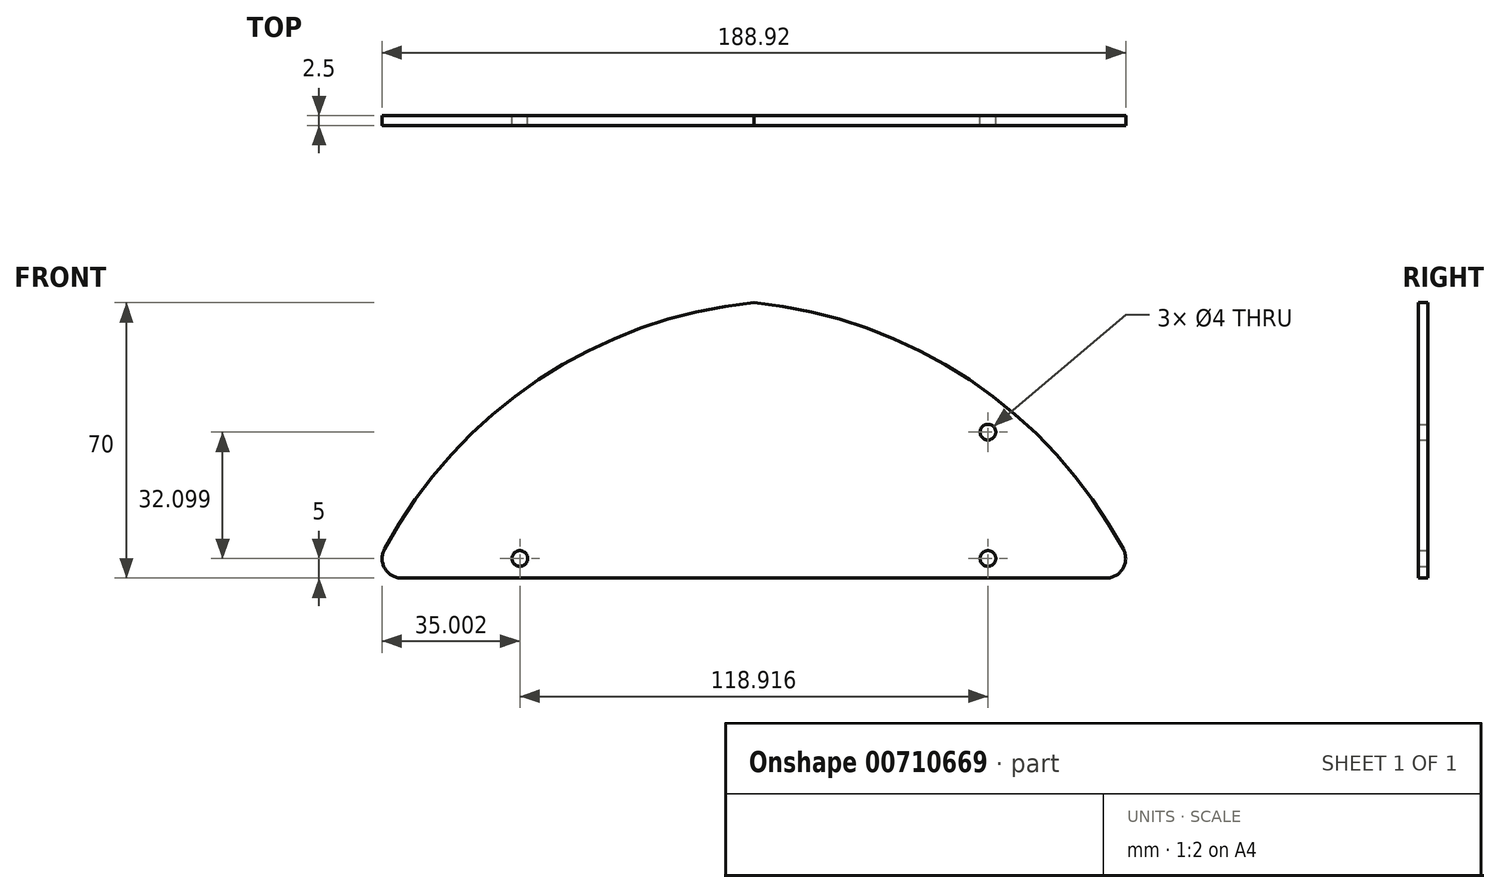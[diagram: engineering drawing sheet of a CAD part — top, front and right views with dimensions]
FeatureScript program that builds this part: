
annotation { "Feature Type Name" : "Feature", "Feature Type Description" : "" }
export const myFeature = defineFeature(function(context is Context, id is Id, definition is map)
    precondition{}
    {
        {
            var Q0;
            Q0=qCreatedBy(makeId("Front.planeOp"),FACE);
            var sketch = newSketch(context, id + "F0", { "sketchPlane" : qUnion([Q0])});
            skLineSegment(sketch, "E0", {"start": v(0, 0) * mm, "end": v(89.46, 0) * mm});
            skArc(sketch, "E1", {"start": v(93.86, 7.37) * mm, "mid": v(54.75, 50.4) * mm, "end": v(0, 70) * mm});
            skPoint(sketch, "E2.visualSharp", {"position": v(-97.5, 0) * mm});
            skPoint(sketch, "E3.visualSharp", {"position": v(97.5, 0) * mm});
            skArc(sketch, "E3.filletArc", {"start": v(89.46, 0) * mm, "mid": v(93.75, 2.43) * mm, "end": v(93.86, 7.37) * mm});
            skCircle(sketch, "E4", {"center": v(59.46, 5) * mm, "radius": 2 * mm});
            skPoint(sketch, "E5.orphan", {"position": v(0, 5) * mm});
            skLineSegment(sketch, "E6", {"start": v(0, 5) * mm, "end": v(0, 0) * mm});
            skArc(sketch, "E7.MirrorCS", {"start": v(-93.86, 7.37) * mm, "mid": v(-54.75, 50.4) * mm, "end": v(0, 70) * mm});
            skLineSegment(sketch, "E8.MirrorCS", {"start": v(0, 0) * mm, "end": v(-89.46, 0) * mm});
            skArc(sketch, "E9.MirrorCS", {"start": v(-89.46, 0) * mm, "mid": v(-93.75, 2.43) * mm, "end": v(-93.86, 7.37) * mm});
            skCircle(sketch, "E10.MirrorC", {"center": v(-59.46, 5) * mm, "radius": 2 * mm});
            skLineSegment(sketch, "E11", {"start": v(59.46, 39.69) * mm, "end": v(59.46, 39.1) * mm});
            skLineSegment(sketch, "E12.trimOffspring", {"start": v(59.46, 39.1) * mm, "end": v(59.46, 39.69) * mm});
            skPoint(sketch, "E13.orphan", {"position": v(59.46, 31.69) * mm});
            skCircle(sketch, "E14", {"center": v(59.46, 37.1) * mm, "radius": 2 * mm});
            skPoint(sketch, "E15.orphan", {"position": v(59.46, 47.1) * mm});
            skSolve(sketch);
        }
        {
            var Q0;
            Q0 = qSketchRegion(id + "F0", true);
            extrude(context, id + "F1", {"entities" : qUnion([Q0]), "depth" : 2.5 * mm, "offsetDistance" : 25 * mm});
        }
    });
